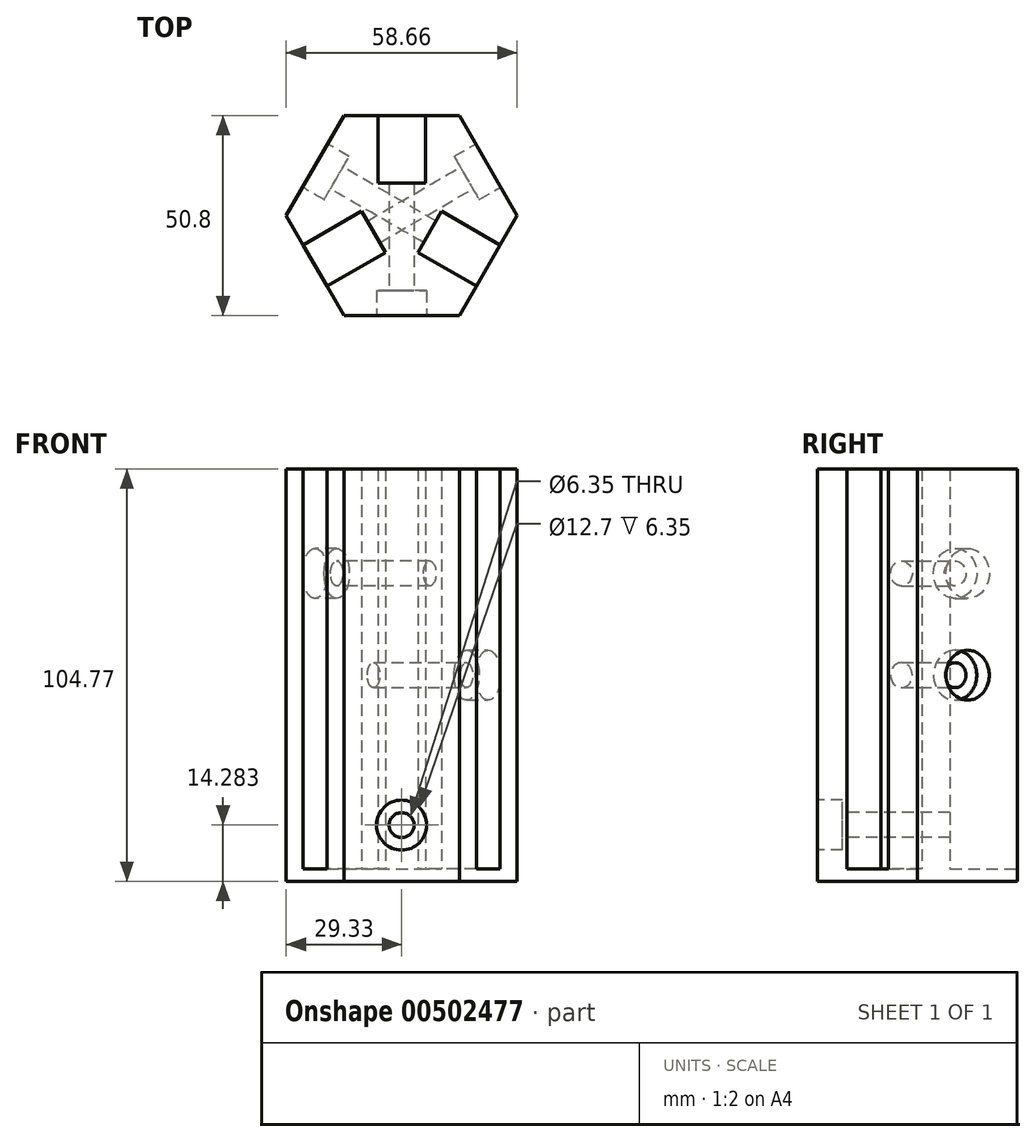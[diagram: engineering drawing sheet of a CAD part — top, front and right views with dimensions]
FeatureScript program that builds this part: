
annotation { "Feature Type Name" : "Feature", "Feature Type Description" : "" }
export const myFeature = defineFeature(function(context is Context, id is Id, definition is map)
    precondition{}
    {
        {
            var Q0;
            Q0=qCreatedBy(makeId("Top.planeOp"),FACE);
            var sketch = newSketch(context, id + "F0", { "sketchPlane" : qUnion([Q0])});
            skCircle(sketch, "E0.cCircle", {"center": v(0, 0) * mm, "radius": 25.4 * mm, "construction": true});
            skLineSegment(sketch, "E0.0", {"start": v(-14.66, 25.4) * mm, "end": v(14.66, 25.4) * mm});
            skLineSegment(sketch, "E0.1", {"start": v(14.66, 25.4) * mm, "end": v(29.33, 0) * mm});
            skLineSegment(sketch, "E0.2", {"start": v(29.33, 0) * mm, "end": v(14.66, -25.4) * mm});
            skLineSegment(sketch, "E0.3", {"start": v(14.66, -25.4) * mm, "end": v(-14.66, -25.4) * mm});
            skLineSegment(sketch, "E0.4", {"start": v(-14.66, -25.4) * mm, "end": v(-29.33, 0) * mm});
            skLineSegment(sketch, "E0.5", {"start": v(-29.33, 0) * mm, "end": v(-14.66, 25.4) * mm});
            skPoint(sketch, "E0.0.midPoint", {"position": v(0, 25.4) * mm});
            skLineSegment(sketch, "E1.0", {"start": v(0, -25.4) * mm, "end": v(-22, 12.7) * mm});
            skLineSegment(sketch, "E1.1", {"start": v(-22, 12.7) * mm, "end": v(22, 12.7) * mm});
            skLineSegment(sketch, "E1.2", {"start": v(22, 12.7) * mm, "end": v(0, -25.4) * mm});
            skLineSegment(sketch, "E2", {"start": v(0, 0) * mm, "end": v(11, -6.35) * mm, "construction": true});
            skLineSegment(sketch, "E3", {"start": v(0, 0) * mm, "end": v(0, 12.7) * mm, "construction": true});
            skLineSegment(sketch, "E4", {"start": v(0, 0) * mm, "end": v(-11, -6.35) * mm, "construction": true});
            skLineSegment(sketch, "E5", {"start": v(-25.01, -7.48) * mm, "end": v(-6.03, 3.48) * mm});
            skLineSegment(sketch, "E6", {"start": v(25.01, -7.48) * mm, "end": v(6.03, 3.48) * mm});
            skLineSegment(sketch, "E7", {"start": v(18.98, -17.92) * mm, "end": v(0, -6.97) * mm});
            skLineSegment(sketch, "E8", {"start": v(0, -6.97) * mm, "end": v(-18.98, -17.92) * mm});
            skLineSegment(sketch, "E9", {"start": v(-6.03, 3.48) * mm, "end": v(-6.03, 25.4) * mm});
            skLineSegment(sketch, "E10", {"start": v(6.03, 3.48) * mm, "end": v(6.03, 25.4) * mm});
            skCircle(sketch, "E11.cCircle", {"center": v(0, 0) * mm, "radius": 6.97 * mm, "construction": true});
            skLineSegment(sketch, "E11.0", {"start": v(0, -6.97) * mm, "end": v(-6.03, 3.48) * mm});
            skLineSegment(sketch, "E11.1", {"start": v(-6.03, 3.48) * mm, "end": v(6.03, 3.48) * mm});
            skLineSegment(sketch, "E11.2", {"start": v(6.03, 3.48) * mm, "end": v(0, -6.97) * mm});
            skLineSegment(sketch, "E12", {"start": v(-10.16, 1.1) * mm, "end": v(-4.12, -9.35) * mm});
            skLineSegment(sketch, "E13", {"start": v(4.12, -9.35) * mm, "end": v(10.16, 1.1) * mm});
            skLineSegment(sketch, "E14", {"start": v(-6.03, 8.25) * mm, "end": v(6.03, 8.25) * mm});
            skSolve(sketch);
        }
        {
            var Q0;
            {var subQ0=sQuery(id+"F0.wireOp",EDGE,"E9");var subQ1=sQuery(id+"F0.wireOp",EDGE,"E0.0");var subQ2=makeQuery(id+"F0.imprint","INTERSECT",VERTEX,{"derivedFrom":[subQ1,subQ0]});Q0=makeQuery(id+"F0.imprint","IMPRINT",FACE,{"disambiguationData":[TD([[makeQuery(id+"F0.imprint","IMPRINT",EDGE,{"disambiguationData":[TD([[subQ2,-1.0]])],"derivedFrom":subQ1}),-1.0]])]});}
            var Q1;
            {var subQ5=sQuery(id+"F0.wireOp",EDGE,"E11.1");Q1=makeQuery(id+"F0.imprint","IMPRINT",FACE,{"disambiguationData":[TD([[makeQuery(id+"F0.imprint","IMPRINT",EDGE,{"derivedFrom":subQ5}),1.0]])]});}
            var Q2;
            {var subQ0=sQuery(id+"F0.wireOp",EDGE,"E0.1");var subQ1=sQuery(id+"F0.wireOp",EDGE,"E0.0");var subQ2=makeQuery(id+"F0.imprint","INTERSECT",VERTEX,{"derivedFrom":[subQ1,subQ0]});Q2=makeQuery(id+"F0.imprint","IMPRINT",FACE,{"disambiguationData":[TD([[makeQuery(id+"F0.imprint","IMPRINT",EDGE,{"disambiguationData":[TD([[subQ2,1.0]])],"derivedFrom":subQ1}),-1.0]])]});}
            var Q3;
            {var subQ1=sQuery(id+"F0.wireOp",EDGE,"E1.1");var subQ3=sQuery(id+"F0.wireOp",EDGE,"E10");var subQ4=makeQuery(id+"F0.imprint","INTERSECT",VERTEX,{"derivedFrom":[subQ1,subQ3]});Q3=makeQuery(id+"F0.imprint","IMPRINT",FACE,{"disambiguationData":[TD([[makeQuery(id+"F0.imprint","IMPRINT",EDGE,{"disambiguationData":[TD([[subQ4,-1.0]])],"derivedFrom":subQ1}),-1.0]])]});}
            var Q4;
            {var subQ0=sQuery(id+"F0.wireOp",EDGE,"E0.2");var subQ1=sQuery(id+"F0.wireOp",EDGE,"E0.1");var subQ2=makeQuery(id+"F0.imprint","INTERSECT",VERTEX,{"derivedFrom":[subQ1,subQ0]});Q4=makeQuery(id+"F0.imprint","IMPRINT",FACE,{"disambiguationData":[TD([[makeQuery(id+"F0.imprint","IMPRINT",EDGE,{"disambiguationData":[TD([[subQ2,-1.0]])],"derivedFrom":subQ0}),-1.0]])]});}
            var Q5;
            {var subQ0=sQuery(id+"F0.wireOp",EDGE,"E6");var subQ1=sQuery(id+"F0.wireOp",EDGE,"E0.2");var subQ2=makeQuery(id+"F0.imprint","INTERSECT",VERTEX,{"derivedFrom":[subQ1,subQ0]});Q5=makeQuery(id+"F0.imprint","IMPRINT",FACE,{"disambiguationData":[TD([[makeQuery(id+"F0.imprint","IMPRINT",EDGE,{"disambiguationData":[TD([[subQ2,-1.0]])],"derivedFrom":subQ1}),-1.0]])]});}
            var Q6;
            {var subQ1=sQuery(id+"F0.wireOp",EDGE,"E1.0");var subQ3=sQuery(id+"F0.wireOp",EDGE,"E8");var subQ4=makeQuery(id+"F0.imprint","INTERSECT",VERTEX,{"derivedFrom":[subQ1,subQ3]});Q6=makeQuery(id+"F0.imprint","IMPRINT",FACE,{"disambiguationData":[TD([[makeQuery(id+"F0.imprint","IMPRINT",EDGE,{"disambiguationData":[TD([[subQ4,1.0]])],"derivedFrom":subQ1}),-1.0]])]});}
            var Q7;
            {var subQ0=sQuery(id+"F0.wireOp",EDGE,"E5");var subQ1=sQuery(id+"F0.wireOp",EDGE,"E0.4");var subQ2=makeQuery(id+"F0.imprint","INTERSECT",VERTEX,{"derivedFrom":[subQ1,subQ0]});Q7=makeQuery(id+"F0.imprint","IMPRINT",FACE,{"disambiguationData":[TD([[makeQuery(id+"F0.imprint","IMPRINT",EDGE,{"disambiguationData":[TD([[subQ2,1.0]])],"derivedFrom":subQ1}),-1.0]])]});}
            var Q8;
            {var subQ0=sQuery(id+"F0.wireOp",EDGE,"E0.5");var subQ1=sQuery(id+"F0.wireOp",EDGE,"E0.4");var subQ2=makeQuery(id+"F0.imprint","INTERSECT",VERTEX,{"derivedFrom":[subQ1,subQ0]});Q8=makeQuery(id+"F0.imprint","IMPRINT",FACE,{"disambiguationData":[TD([[makeQuery(id+"F0.imprint","IMPRINT",EDGE,{"disambiguationData":[TD([[subQ2,1.0]])],"derivedFrom":subQ1}),-1.0]])]});}
            var Q9;
            {var subQ0=sQuery(id+"F0.wireOp",EDGE,"E0.5");var subQ1=sQuery(id+"F0.wireOp",EDGE,"E0.0");var subQ2=makeQuery(id+"F0.imprint","INTERSECT",VERTEX,{"derivedFrom":[subQ1,subQ0]});Q9=makeQuery(id+"F0.imprint","IMPRINT",FACE,{"disambiguationData":[TD([[makeQuery(id+"F0.imprint","IMPRINT",EDGE,{"disambiguationData":[TD([[subQ2,-1.0]])],"derivedFrom":subQ1}),-1.0]])]});}
            var Q10;
            {var subQ0=sQuery(id+"F0.wireOp",EDGE,"E0.4");var subQ1=sQuery(id+"F0.wireOp",EDGE,"E0.3");var subQ2=makeQuery(id+"F0.imprint","INTERSECT",VERTEX,{"derivedFrom":[subQ1,subQ0]});Q10=makeQuery(id+"F0.imprint","IMPRINT",FACE,{"disambiguationData":[TD([[makeQuery(id+"F0.imprint","IMPRINT",EDGE,{"disambiguationData":[TD([[subQ2,-1.0]])],"derivedFrom":subQ0}),-1.0]])]});}
            var Q11;
            {var subQ0=sQuery(id+"F0.wireOp",EDGE,"E0.3");var subQ1=sQuery(id+"F0.wireOp",EDGE,"E0.2");var subQ2=makeQuery(id+"F0.imprint","INTERSECT",VERTEX,{"derivedFrom":[subQ1,subQ0]});Q11=makeQuery(id+"F0.imprint","IMPRINT",FACE,{"disambiguationData":[TD([[makeQuery(id+"F0.imprint","IMPRINT",EDGE,{"disambiguationData":[TD([[subQ2,1.0]])],"derivedFrom":subQ1}),-1.0]])]});}
            var Q12;
            {var subQ1=sQuery(id+"F0.wireOp",EDGE,"E1.0");var subQ3=sQuery(id+"F0.wireOp",EDGE,"E5");var subQ4=makeQuery(id+"F0.imprint","INTERSECT",VERTEX,{"derivedFrom":[subQ1,subQ3]});Q12=makeQuery(id+"F0.imprint","IMPRINT",FACE,{"disambiguationData":[TD([[makeQuery(id+"F0.imprint","IMPRINT",EDGE,{"disambiguationData":[TD([[subQ4,-1.0]])],"derivedFrom":subQ1}),-1.0]])]});}
            var Q13;
            {var subQ5=sQuery(id+"F0.wireOp",EDGE,"E11.0");Q13=makeQuery(id+"F0.imprint","IMPRINT",FACE,{"disambiguationData":[TD([[makeQuery(id+"F0.imprint","IMPRINT",EDGE,{"derivedFrom":subQ5}),1.0]])]});}
            var Q14;
            {var subQ5=sQuery(id+"F0.wireOp",EDGE,"E11.2");Q14=makeQuery(id+"F0.imprint","IMPRINT",FACE,{"disambiguationData":[TD([[makeQuery(id+"F0.imprint","IMPRINT",EDGE,{"derivedFrom":subQ5}),1.0]])]});}
            var Q15;
            Q15=makeQuery(id+"F0.imprint","IMPRINT",FACE,{"disambiguationData":[TD([[makeQuery(id+"F0.imprint","IMPRINT",EDGE,{"derivedFrom":sQuery(id+"F0.wireOp",EDGE,"E11.0")}),-1.0]])]});
            var Q16;
            Q16=makeQuery(id+"F2.opExtrude","SWEPT_FACE",FACE,{"disambiguationData":[OSD([sQuery(id+"F0.wireOp",EDGE,"E6")])]});
            var Q17;
            {var subQ5=sQuery(id+"F0.wireOp",EDGE,"E14");Q17=makeQuery(id+"F0.imprint","IMPRINT",FACE,{"disambiguationData":[TD([[makeQuery(id+"F0.imprint","IMPRINT",EDGE,{"derivedFrom":subQ5}),1.0]])]});}
            var Q18;
            {var subQ5=sQuery(id+"F0.wireOp",EDGE,"E13");Q18=makeQuery(id+"F0.imprint","IMPRINT",FACE,{"disambiguationData":[TD([[makeQuery(id+"F0.imprint","IMPRINT",EDGE,{"derivedFrom":subQ5}),-1.0]])]});}
            var Q19;
            {var subQ5=sQuery(id+"F0.wireOp",EDGE,"E12");Q19=makeQuery(id+"F0.imprint","IMPRINT",FACE,{"disambiguationData":[TD([[makeQuery(id+"F0.imprint","IMPRINT",EDGE,{"derivedFrom":subQ5}),-1.0]])]});}
            extrude(context, id + "F1", {"entities" : qUnion([Q0, Q1, Q2, Q3, Q4, Q5, Q6, Q7, Q8, Q9, Q10, Q11, Q12, Q13, Q14, Q15, Q16, Q17, Q18, Q19]), "oppositeDirection" : true, "depth" : 3.17 * mm});
        }
        {
            var Q0;
            {var subQ0=sQuery(id+"F0.wireOp",EDGE,"E0.5");var subQ1=sQuery(id+"F0.wireOp",EDGE,"E0.0");var subQ2=makeQuery(id+"F0.imprint","INTERSECT",VERTEX,{"derivedFrom":[subQ1,subQ0]});Q0=makeQuery(id+"F0.imprint","IMPRINT",FACE,{"disambiguationData":[TD([[makeQuery(id+"F0.imprint","IMPRINT",EDGE,{"disambiguationData":[TD([[subQ2,-1.0]])],"derivedFrom":subQ1}),-1.0]])]});}
            var Q1;
            {var subQ0=sQuery(id+"F0.wireOp",EDGE,"E0.1");var subQ1=sQuery(id+"F0.wireOp",EDGE,"E0.0");var subQ2=makeQuery(id+"F0.imprint","INTERSECT",VERTEX,{"derivedFrom":[subQ1,subQ0]});Q1=makeQuery(id+"F0.imprint","IMPRINT",FACE,{"disambiguationData":[TD([[makeQuery(id+"F0.imprint","IMPRINT",EDGE,{"disambiguationData":[TD([[subQ2,1.0]])],"derivedFrom":subQ1}),-1.0]])]});}
            var Q2;
            {var subQ0=sQuery(id+"F0.wireOp",EDGE,"E0.2");var subQ1=sQuery(id+"F0.wireOp",EDGE,"E0.1");var subQ2=makeQuery(id+"F0.imprint","INTERSECT",VERTEX,{"derivedFrom":[subQ1,subQ0]});Q2=makeQuery(id+"F0.imprint","IMPRINT",FACE,{"disambiguationData":[TD([[makeQuery(id+"F0.imprint","IMPRINT",EDGE,{"disambiguationData":[TD([[subQ2,-1.0]])],"derivedFrom":subQ0}),-1.0]])]});}
            var Q3;
            {var subQ0=sQuery(id+"F0.wireOp",EDGE,"E0.5");var subQ1=sQuery(id+"F0.wireOp",EDGE,"E0.4");var subQ2=makeQuery(id+"F0.imprint","INTERSECT",VERTEX,{"derivedFrom":[subQ1,subQ0]});Q3=makeQuery(id+"F0.imprint","IMPRINT",FACE,{"disambiguationData":[TD([[makeQuery(id+"F0.imprint","IMPRINT",EDGE,{"disambiguationData":[TD([[subQ2,1.0]])],"derivedFrom":subQ1}),-1.0]])]});}
            var Q4;
            {var subQ1=sQuery(id+"F0.wireOp",EDGE,"E1.1");var subQ3=sQuery(id+"F0.wireOp",EDGE,"E10");var subQ4=makeQuery(id+"F0.imprint","INTERSECT",VERTEX,{"derivedFrom":[subQ1,subQ3]});Q4=makeQuery(id+"F0.imprint","IMPRINT",FACE,{"disambiguationData":[TD([[makeQuery(id+"F0.imprint","IMPRINT",EDGE,{"disambiguationData":[TD([[subQ4,-1.0]])],"derivedFrom":subQ1}),-1.0]])]});}
            var Q5;
            {var subQ1=sQuery(id+"F0.wireOp",EDGE,"E1.0");var subQ3=sQuery(id+"F0.wireOp",EDGE,"E5");var subQ4=makeQuery(id+"F0.imprint","INTERSECT",VERTEX,{"derivedFrom":[subQ1,subQ3]});Q5=makeQuery(id+"F0.imprint","IMPRINT",FACE,{"disambiguationData":[TD([[makeQuery(id+"F0.imprint","IMPRINT",EDGE,{"disambiguationData":[TD([[subQ4,-1.0]])],"derivedFrom":subQ1}),-1.0]])]});}
            var Q6;
            {var subQ1=sQuery(id+"F0.wireOp",EDGE,"E1.0");var subQ3=sQuery(id+"F0.wireOp",EDGE,"E8");var subQ4=makeQuery(id+"F0.imprint","INTERSECT",VERTEX,{"derivedFrom":[subQ1,subQ3]});Q6=makeQuery(id+"F0.imprint","IMPRINT",FACE,{"disambiguationData":[TD([[makeQuery(id+"F0.imprint","IMPRINT",EDGE,{"disambiguationData":[TD([[subQ4,1.0]])],"derivedFrom":subQ1}),-1.0]])]});}
            var Q7;
            {var subQ0=sQuery(id+"F0.wireOp",EDGE,"E0.3");var subQ1=sQuery(id+"F0.wireOp",EDGE,"E0.2");var subQ2=makeQuery(id+"F0.imprint","INTERSECT",VERTEX,{"derivedFrom":[subQ1,subQ0]});Q7=makeQuery(id+"F0.imprint","IMPRINT",FACE,{"disambiguationData":[TD([[makeQuery(id+"F0.imprint","IMPRINT",EDGE,{"disambiguationData":[TD([[subQ2,1.0]])],"derivedFrom":subQ1}),-1.0]])]});}
            var Q8;
            {var subQ0=sQuery(id+"F0.wireOp",EDGE,"E0.4");var subQ1=sQuery(id+"F0.wireOp",EDGE,"E0.3");var subQ2=makeQuery(id+"F0.imprint","INTERSECT",VERTEX,{"derivedFrom":[subQ1,subQ0]});Q8=makeQuery(id+"F0.imprint","IMPRINT",FACE,{"disambiguationData":[TD([[makeQuery(id+"F0.imprint","IMPRINT",EDGE,{"disambiguationData":[TD([[subQ2,-1.0]])],"derivedFrom":subQ0}),-1.0]])]});}
            var Q9;
            {var subQ0=sQuery(id+"F0.wireOp",EDGE,"E11.0");Q9=makeQuery(id+"F0.imprint","IMPRINT",FACE,{"disambiguationData":[TD([[makeQuery(id+"F0.imprint","IMPRINT",EDGE,{"derivedFrom":subQ0}),1.0]])]});}
            var Q10;
            {var subQ0=sQuery(id+"F0.wireOp",EDGE,"E11.2");Q10=makeQuery(id+"F0.imprint","IMPRINT",FACE,{"disambiguationData":[TD([[makeQuery(id+"F0.imprint","IMPRINT",EDGE,{"derivedFrom":subQ0}),1.0]])]});}
            var Q11;
            {var subQ0=sQuery(id+"F0.wireOp",EDGE,"E11.1");Q11=makeQuery(id+"F0.imprint","IMPRINT",FACE,{"disambiguationData":[TD([[makeQuery(id+"F0.imprint","IMPRINT",EDGE,{"derivedFrom":subQ0}),1.0]])]});}
            var Q12;
            Q12=makeQuery(id+"F0.imprint","IMPRINT",FACE,{"disambiguationData":[TD([[makeQuery(id+"F0.imprint","IMPRINT",EDGE,{"derivedFrom":sQuery(id+"F0.wireOp",EDGE,"E11.0")}),-1.0]])]});
            extrude(context, id + "F2", {"entities" : qUnion([Q0, Q1, Q2, Q3, Q4, Q5, Q6, Q7, Q8, Q9, Q10, Q11, Q12]), "operationType" : NewBodyOperationType.ADD, "depth" : 101.6 * mm});
        }
        {
            var Q0;
            {var subQ0=sQuery(id+"F0.wireOp",EDGE,"E0.3");Q0=makeQuery(id+"F2.boolean.opBoolean","MERGE",FACE,{"derivedFrom":[makeQuery(id+"F1.opExtrude","SWEPT_FACE",FACE,{"disambiguationData":[OSD([subQ0])]}),makeQuery(id+"F2.opExtrude","SWEPT_FACE",FACE,{"disambiguationData":[OSD([subQ0])]})]});}
            var sketch = newSketch(context, id + "F3", { "sketchPlane" : qUnion([Q0])});
            skPoint(sketch, "E15", {"position": v(0, 11.11) * mm});
            skSolve(sketch);
        }
        {
            var Q0;
            {var subQ0=sQuery(id+"F0.wireOp",EDGE,"E0.1");Q0=makeQuery(id+"F2.boolean.opBoolean","MERGE",FACE,{"derivedFrom":[makeQuery(id+"F1.opExtrude","SWEPT_FACE",FACE,{"disambiguationData":[OSD([subQ0])]}),makeQuery(id+"F2.opExtrude","SWEPT_FACE",FACE,{"disambiguationData":[OSD([subQ0])]})]});}
            var sketch = newSketch(context, id + "F4", { "sketchPlane" : qUnion([Q0])});
            skPoint(sketch, "E16", {"position": v(0, 49.21) * mm});
            skPoint(sketch, "E16.positionSnap0", {"position": v(-14.66, 49.21) * mm});
            skSolve(sketch);
        }
        {
            var Q0;
            {var subQ0=sQuery(id+"F0.wireOp",EDGE,"E0.5");Q0=makeQuery(id+"F2.boolean.opBoolean","MERGE",FACE,{"derivedFrom":[makeQuery(id+"F1.opExtrude","SWEPT_FACE",FACE,{"disambiguationData":[OSD([subQ0])]}),makeQuery(id+"F2.opExtrude","SWEPT_FACE",FACE,{"disambiguationData":[OSD([subQ0])]})]});}
            var sketch = newSketch(context, id + "F5", { "sketchPlane" : qUnion([Q0])});
            skPoint(sketch, "E17", {"position": v(0, 75.06) * mm});
            skPoint(sketch, "E17.positionSnap0", {"position": v(-14.66, 49.21) * mm});
            skPoint(sketch, "E17.positionSnap1", {"position": v(0, 101.6) * mm});
            skSolve(sketch);
        }
        {
            var Q0;
            Q0=sQuery(id+"F3.wireOp",VERTEX,"E15");
            var Q1;
            Q1=sQuery(id+"F4.wireOp",VERTEX,"E16");
            var Q2;
            Q2=sQuery(id+"F5.wireOp",VERTEX,"E17");
            var Q3;
            Q3=makeQuery(id+"F1.opExtrude","SWEPT_BODY",BODY,{"disambiguationData":[OSD([sQuery(id+"F0.wireOp",EDGE,"E0.0"),sQuery(id+"F0.wireOp",EDGE,"E0.1"),sQuery(id+"F0.wireOp",EDGE,"E0.2"),sQuery(id+"F0.wireOp",EDGE,"E0.3"),sQuery(id+"F0.wireOp",EDGE,"E0.4"),sQuery(id+"F0.wireOp",EDGE,"E0.5")])]});
            hole(context, id + "F6", {"style" : HoleStyle.C_BORE, "endStyle" : HoleEndStyle.THROUGH, "holeDiameter" : 6.35 * mm, "cBoreDiameter" : 12.7 * mm, "cBoreDepth" : 6.35 * mm, "isTappedThrough" : true, "tappedDepth" : 12.7 * mm, "tapClearance" : 3, "locations" : qUnion([Q0, Q1, Q2]), "scope" : qUnion([Q3])});
        }
    });
